# Revit family: STH20961BR_27_40_STH20961PTO_27
name_source: partatom
category: Luminárias
units: mm (PartAtom-declared; Revit-internal decimal feet)

## family parameters
Compartilhado = Não
Corte com vazios quando carregada = Não
Cota do conector redondo = Utilizar diâmetro
Fonte luminosa = Sim
Hospedeiro = Forro
Manter orientação da anotação = Não
Número OmniClass = 23.80.70.11
Ponto de cálculo do ambiente = Não
Sempre na vertical = Sim
Tipo de parte = Normal
Título OmniClass = Luminaries for Internal Lighting

## types (3) — shared parameters
Altura = 0.03 m
Comprimento = 1.01 m
Dimerização = Não dimerizável
Fabricante = Stella
Filtro de cor = 16777215
Grau de proteção (IP) = IP20
IRC (Índice de reprodução de cores) = >93 (R9 >60)
Largura = 0.03 m
Modelo = Archi
Tensão Elétrica = 24V
Troca de temperatura da cor de lâmpada com esmaecimento = <Nenhum>
URL = https://stella.com.br
Ângulo de Abertura = 110°
Ângulo de inclinação = 90.00°
zero-valued in all types: Elevação padrão

## per-type parameters (varying)
| type | Arquivo de rede fotométrica | Estrutura | Fluxo Luminoso | Luminoso | Potência | Referência | Temperatura da cor (K) |
| STH20961BR/27 - BRANCO - 1m - 2700K - 570lm - 110° | STELLA - STH20961BR-27 - ARCHI - PERFIL DE SOBREPOR PLANO 24V.ies | Al - Branco | 570 lm | Luminoso - 2700K | 12 W | STH20961BR/27 - BRANCO - 1m | 2700 K |
| STH20961BR/40 - BRANCO - 1m - 4000K - 570lm - 110° | STELLA - STH20961BR-40 - PERFIL DE SOBREPOR ARCHI 1m.ies | Al - Branco | 570 lm | Luminoso - 4000K | 12 W | STH20961BR/40 - BRANCO - 1m | 4000 K |
| STH20961PTO/27 - PRETO - 1m - 2700K - 420lm - 110° | STELLA - STH20961PTO-27 - PERFIL DE SOBREPOR PLANO 24Vcc.ies | Al - Preto | 420 lm | Luminoso - 2700K | 14 W | STH20961PTO/27 - PRETO - 1m | 2700 K |
